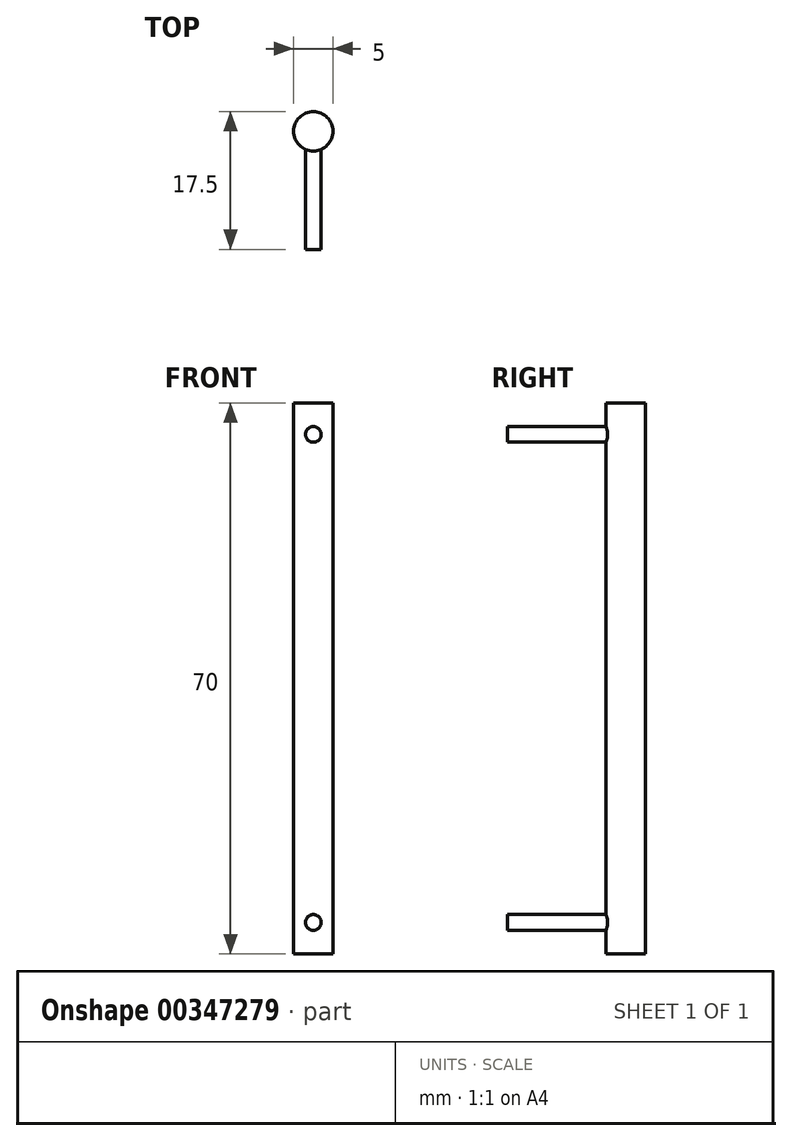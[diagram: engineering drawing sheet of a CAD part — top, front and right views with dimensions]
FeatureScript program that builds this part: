
annotation { "Feature Type Name" : "Feature", "Feature Type Description" : "" }
export const myFeature = defineFeature(function(context is Context, id is Id, definition is map)
    precondition{}
    {
        {
            var Q0;
            Q0=qCreatedBy(makeId("Top.planeOp"),FACE);
            var sketch = newSketch(context, id + "F0", { "sketchPlane" : qUnion([Q0])});
            skCircle(sketch, "E0", {"center": v(0, 0) * mm, "radius": 2.5 * mm});
            skSolve(sketch);
        }
        {
            var Q0;
            Q0=makeQuery(id+"F0.imprint","IMPRINT",FACE,{"disambiguationData":[TD([[makeQuery(id+"F0.imprint","IMPRINT",EDGE,{"derivedFrom":sQuery(id+"F0.wireOp",EDGE,"E0")}),1.0]])]});
            extrude(context, id + "F1", {"entities" : qUnion([Q0]), "depth" : 70 * mm});
        }
        {
            var Q0;
            Q0=qCreatedBy(makeId("Front.planeOp"),FACE);
            var sketch = newSketch(context, id + "F2", { "sketchPlane" : qUnion([Q0])});
            skCircle(sketch, "E1", {"center": v(0, 66) * mm, "radius": 1 * mm});
            skCircle(sketch, "E2", {"center": v(0, 4) * mm, "radius": 1 * mm});
            skSolve(sketch);
        }
        {
            var Q0;
            Q0 = qSketchRegion(id + "F2", true);
            extrude(context, id + "F3", {"entities" : qUnion([Q0]), "operationType" : NewBodyOperationType.ADD, "depth" : 15 * mm});
        }
    });
